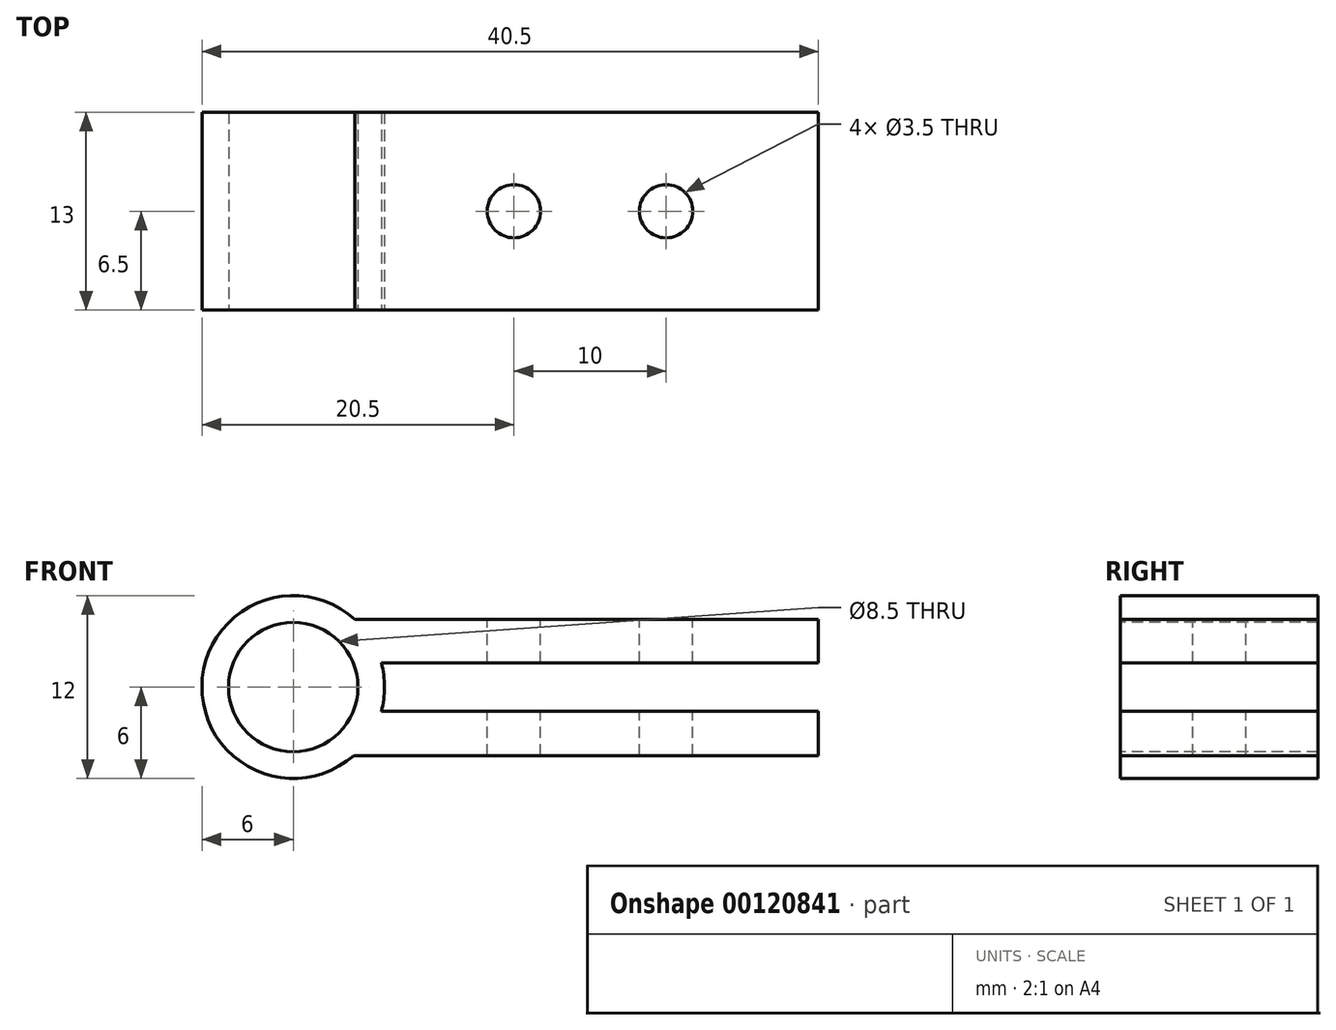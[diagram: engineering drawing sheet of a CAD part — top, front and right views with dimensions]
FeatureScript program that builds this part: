
annotation { "Feature Type Name" : "Feature", "Feature Type Description" : "" }
export const myFeature = defineFeature(function(context is Context, id is Id, definition is map)
    precondition{}
    {
        {
            var Q0;
            Q0=qCreatedBy(makeId("Front.planeOp"),FACE);
            var sketch = newSketch(context, id + "F0", { "sketchPlane" : qUnion([Q0])});
            skCircle(sketch, "E0", {"center": v(0, 0) * mm, "radius": 6 * mm});
            skCircle(sketch, "E1", {"center": v(0, 0) * mm, "radius": 4.25 * mm});
            skSolve(sketch);
        }
        {
            var Q0;
            Q0=makeQuery(id+"F0.imprint","IMPRINT",FACE,{"disambiguationData":[TD([[makeQuery(id+"F0.imprint","IMPRINT",EDGE,{"derivedFrom":sQuery(id+"F0.wireOp",EDGE,"E0")}),1.0]])]});
            extrude(context, id + "F1", {"entities" : qUnion([Q0]), "oppositeDirection" : true, "depth" : 13 * mm});
        }
        {
            var Q0;
            Q0=qCreatedBy(makeId("Right.planeOp"),FACE);
            var sketch = newSketch(context, id + "F2", { "sketchPlane" : qUnion([Q0])});
            skLineSegment(sketch, "E2.bottom", {"start": v(0, 4.43) * mm, "end": v(13, 4.43) * mm});
            skLineSegment(sketch, "E2.top", {"start": v(0, 1.6) * mm, "end": v(13, 1.6) * mm});
            skLineSegment(sketch, "E2.left", {"start": v(0, 4.43) * mm, "end": v(0, 1.6) * mm});
            skLineSegment(sketch, "E2.right", {"start": v(13, 4.43) * mm, "end": v(13, 1.6) * mm});
            skLineSegment(sketch, "E3.bottom", {"start": v(0, -1.6) * mm, "end": v(13, -1.6) * mm});
            skLineSegment(sketch, "E3.top", {"start": v(0, -4.5) * mm, "end": v(13, -4.5) * mm});
            skLineSegment(sketch, "E3.left", {"start": v(0, -1.6) * mm, "end": v(0, -4.5) * mm});
            skLineSegment(sketch, "E3.right", {"start": v(13, -1.6) * mm, "end": v(13, -4.5) * mm});
            skSolve(sketch);
        }
        {
            var Q0;
            Q0 = qSketchRegion(id + "F2", true);
            extrude(context, id + "F3", {"entities" : qUnion([Q0]), "operationType" : NewBodyOperationType.ADD, "depth" : 34.5 * mm});
        }
        {
            var Q0;
            Q0=makeQuery(id+"F3.boolean.opBoolean","MERGE",FACE,{"derivedFrom":[makeQuery(id+"F1.opExtrude","CAP_FACE",FACE,{"disambiguationData":[OSD([sQuery(id+"F0.wireOp",EDGE,"E0"),sQuery(id+"F0.wireOp",EDGE,"E1")])],"isStart":false}),makeQuery(id+"F3.opExtrude","SWEPT_FACE",FACE,{"disambiguationData":[OSD([sQuery(id+"F2.wireOp",EDGE,"E2.right")])]}),makeQuery(id+"F3.opExtrude","SWEPT_FACE",FACE,{"disambiguationData":[OSD([sQuery(id+"F2.wireOp",EDGE,"E3.right")])]})]});
            var sketch = newSketch(context, id + "F4", { "sketchPlane" : qUnion([Q0])});
            skCircle(sketch, "E4", {"center": v(0, 0) * mm, "radius": 4.25 * mm});
            skSolve(sketch);
        }
        {
            var Q0;
            Q0 = qSketchRegion(id + "F4", true);
            extrude(context, id + "F5", {"entities" : qUnion([Q0]), "operationType" : NewBodyOperationType.REMOVE, "endBound" : BoundingType.THROUGH_ALL, "oppositeDirection" : true, "depth" : 25 * mm});
        }
        {
            var Q0;
            Q0=makeQuery(id+"F3.opExtrude","SWEPT_FACE",FACE,{"disambiguationData":[OSD([sQuery(id+"F2.wireOp",EDGE,"E2.bottom")])]});
            var sketch = newSketch(context, id + "F6", { "sketchPlane" : qUnion([Q0])});
            skCircle(sketch, "E5", {"center": v(14.5, 6.5) * mm, "radius": 1.75 * mm});
            skCircle(sketch, "E6", {"center": v(24.5, 6.5) * mm, "radius": 1.75 * mm});
            skSolve(sketch);
        }
        {
            var Q0;
            Q0 = qSketchRegion(id + "F6", true);
            var Q1;
            Q1=makeQuery(id+"F3.opExtrude","SWEPT_FACE",FACE,{"disambiguationData":[OSD([sQuery(id+"F2.wireOp",EDGE,"E3.top")])]});
            extrude(context, id + "F7", {"entities" : qUnion([Q0]), "operationType" : NewBodyOperationType.REMOVE, "endBound" : BoundingType.UP_TO_SURFACE, "oppositeDirection" : true, "endBoundEntityFace" : qUnion([Q1]), "depth" : 25 * mm});
        }
    });
